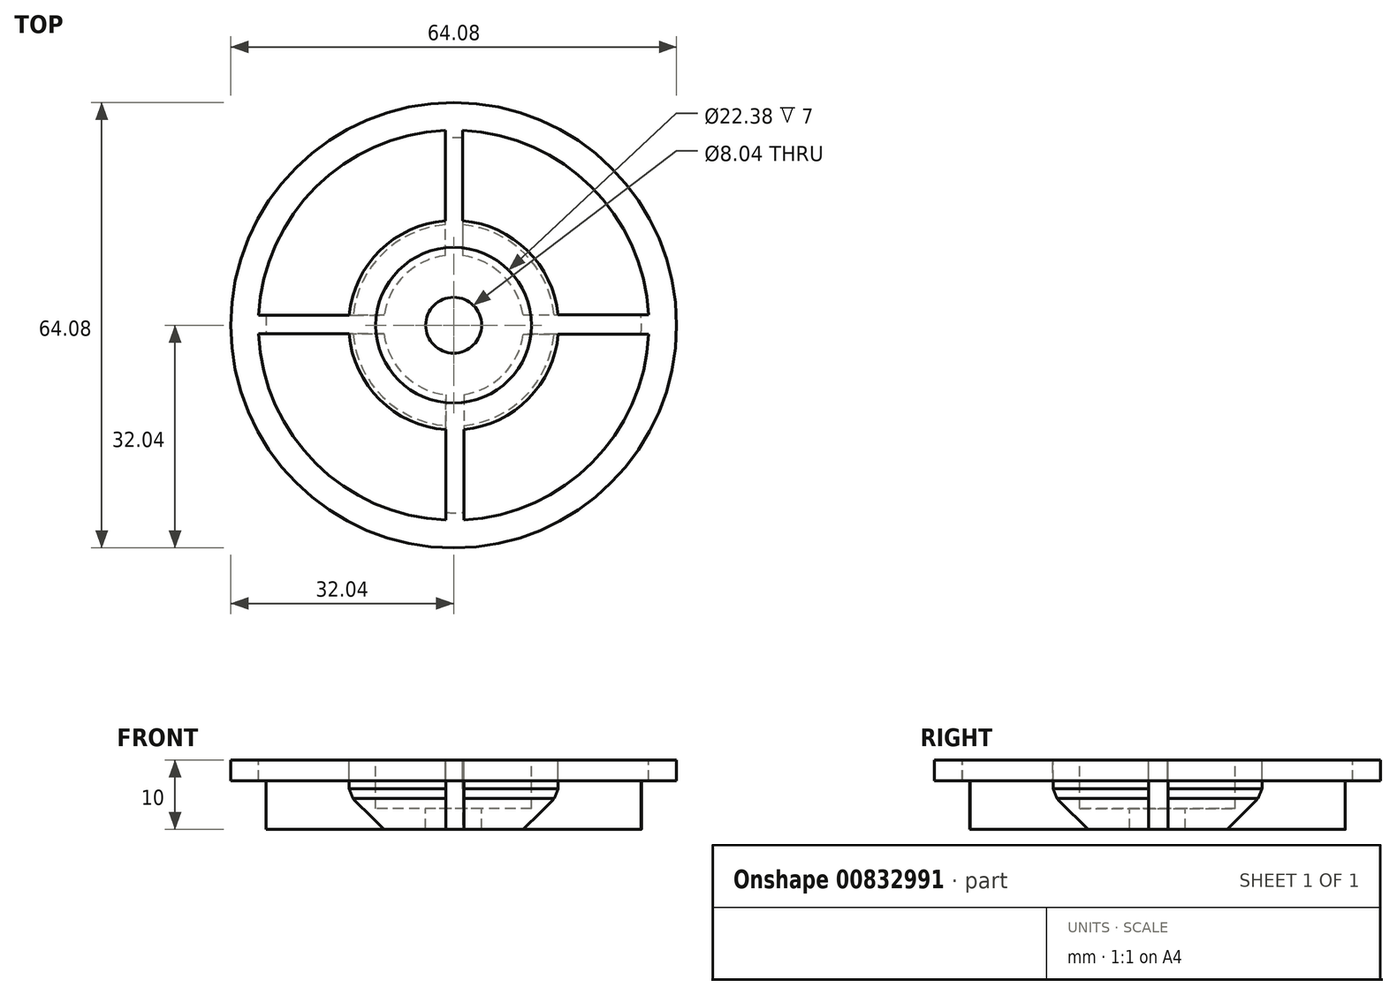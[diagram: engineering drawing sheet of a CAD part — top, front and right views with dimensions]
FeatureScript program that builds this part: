
annotation { "Feature Type Name" : "Feature", "Feature Type Description" : "" }
export const myFeature = defineFeature(function(context is Context, id is Id, definition is map)
    precondition{}
    {
        {
            var Q0;
            Q0=qCreatedBy(makeId("Top.planeOp"),FACE);
            var sketch = newSketch(context, id + "F0", { "sketchPlane" : qUnion([Q0])});
            skCircle(sketch, "E0", {"center": v(0, 0) * mm, "radius": 26.99 * mm});
            skSolve(sketch);
        }
        {
            var Q0;
            Q0 = qSketchRegion(id + "F0", true);
            extrude(context, id + "F1", {"entities" : qUnion([Q0]), "depth" : 7 * mm, "offsetDistance" : 25 * mm});
        }
        {
            var Q0;
            Q0=makeQuery(id+"F1.opExtrude","CAP_FACE",FACE,{"disambiguationData":[OSD([sQuery(id+"F0.wireOp",EDGE,"E0")])],"isStart":false});
            var sketch = newSketch(context, id + "F2", { "sketchPlane" : qUnion([Q0])});
            skCircle(sketch, "E1", {"center": v(0, 0) * mm, "radius": 32.04 * mm});
            skSolve(sketch);
        }
        {
            var Q0;
            Q0=makeQuery(id+"F2.imprint","IMPRINT",FACE,{"disambiguationData":[TD([[makeQuery(id+"F2.imprint","IMPRINT",EDGE,{"derivedFrom":sQuery(id+"F2.wireOp",EDGE,"E1")}),1.0]])]});
            var Q1;
            Q1=makeQuery(id+"F2.imprint","IMPRINT",FACE,{"disambiguationData":[TD([[makeQuery(id+"F2.imprint","IMPRINT",EDGE,{"derivedFrom":makeQuery(id+"F1.opExtrude","CAP_EDGE",EDGE,{"disambiguationData":[OSD([sQuery(id+"F0.wireOp",EDGE,"E0")])],"isStart":false})}),1.0]])]});
            extrude(context, id + "F3", {"entities" : qUnion([Q0, Q1]), "operationType" : NewBodyOperationType.ADD, "depth" : 3 * mm, "offsetDistance" : 25 * mm});
        }
        {
            var Q0;
            Q0=makeQuery(id+"F3.opExtrude","CAP_FACE",FACE,{"disambiguationData":[OSD([sQuery(id+"F2.wireOp",EDGE,"E1")])],"isStart":false});
            var sketch = newSketch(context, id + "F4", { "sketchPlane" : qUnion([Q0])});
            skCircle(sketch, "E2", {"center": v(0, 0) * mm, "radius": 11.2 * mm});
            skSolve(sketch);
        }
        {
            var Q0;
            Q0 = qSketchRegion(id + "F4", true);
            extrude(context, id + "F5", {"entities" : qUnion([Q0]), "operationType" : NewBodyOperationType.REMOVE, "oppositeDirection" : true, "depth" : 7 * mm, "offsetDistance" : 25 * mm});
        }
        {
            var Q0;
            Q0=makeQuery(id+"F5.boolean.opBoolean","COPY",FACE,{"derivedFrom":makeQuery(id+"F5.opExtrude","CAP_FACE",FACE,{"disambiguationData":[OSD([sQuery(id+"F4.wireOp",EDGE,"E2")])],"isStart":false})});
            var sketch = newSketch(context, id + "F6", { "sketchPlane" : qUnion([Q0])});
            skCircle(sketch, "E3", {"center": v(0, 0) * mm, "radius": 4.02 * mm});
            skSolve(sketch);
        }
        {
            var Q0;
            Q0 = qSketchRegion(id + "F6", true);
            extrude(context, id + "F7", {"entities" : qUnion([Q0]), "operationType" : NewBodyOperationType.REMOVE, "oppositeDirection" : true, "depth" : 25 * mm, "offsetDistance" : 25 * mm});
        }
        {
            var Q0;
            Q0=makeQuery(id+"F3.opExtrude","CAP_FACE",FACE,{"disambiguationData":[OSD([sQuery(id+"F2.wireOp",EDGE,"E1")])],"isStart":false});
            var sketch = newSketch(context, id + "F8", { "sketchPlane" : qUnion([Q0])});
            skArc(sketch, "E4", {"start": v(-15.03, -1.26) * mm, "mid": v(-10.63, -10.7) * mm, "end": v(-1.15, -15.04) * mm});
            skArc(sketch, "E5", {"start": v(-28.04, -1.26) * mm, "mid": v(-19.8, -19.88) * mm, "end": v(-1.15, -28.04) * mm});
            skLineSegment(sketch, "E6", {"start": v(1.48, -15.01) * mm, "end": v(1.48, -28.03) * mm});
            skLineSegment(sketch, "E7", {"start": v(-1.15, -15.04) * mm, "end": v(-1.15, -28.04) * mm});
            skLineSegment(sketch, "E8", {"start": v(15.03, -1.26) * mm, "end": v(28.04, -1.26) * mm});
            skLineSegment(sketch, "E9", {"start": v(15, 1.52) * mm, "end": v(28.02, 1.52) * mm});
            skLineSegment(sketch, "E10", {"start": v(-1.22, 15.03) * mm, "end": v(-1.22, 28.04) * mm});
            skLineSegment(sketch, "E11", {"start": v(1.3, 28.04) * mm, "end": v(1.3, 15.03) * mm});
            skLineSegment(sketch, "E12", {"start": v(-15.01, 1.44) * mm, "end": v(-28.03, 1.44) * mm});
            skLineSegment(sketch, "E13", {"start": v(-28.04, -1.26) * mm, "end": v(-15.03, -1.26) * mm});
            skPoint(sketch, "E14.start.orphan", {"position": v(-15.08, 0) * mm});
            skArc(sketch, "E15.trimOffspring", {"start": v(-1.22, 15.03) * mm, "mid": v(-10.58, 10.74) * mm, "end": v(-15.01, 1.44) * mm});
            skPoint(sketch, "E16.orphan", {"position": v(0, 15.08) * mm});
            skArc(sketch, "E17.trimOffspring", {"start": v(-1.22, 28.04) * mm, "mid": v(-19.77, 19.92) * mm, "end": v(-28.03, 1.44) * mm});
            skArc(sketch, "E18.trimOffspring", {"start": v(15, 1.52) * mm, "mid": v(10.58, 10.74) * mm, "end": v(1.3, 15.03) * mm});
            skPoint(sketch, "E19.start.orphan", {"position": v(15.08, 0) * mm});
            skArc(sketch, "E20.trimOffspring", {"start": v(28.02, 1.52) * mm, "mid": v(19.77, 19.92) * mm, "end": v(1.3, 28.04) * mm});
            skArc(sketch, "E21.trimOffspring", {"start": v(1.48, -28.03) * mm, "mid": v(19.92, -19.77) * mm, "end": v(28.04, -1.26) * mm});
            skPoint(sketch, "E22.start.orphan", {"position": v(0, -15.08) * mm});
            skArc(sketch, "E23.trimOffspring", {"start": v(1.48, -15.01) * mm, "mid": v(10.74, -10.59) * mm, "end": v(15.03, -1.26) * mm});
            skSolve(sketch);
        }
        {
            var Q0;
            Q0=makeQuery(id+"F8.imprint","IMPRINT",FACE,{"disambiguationData":[TD([[makeQuery(id+"F8.imprint","IMPRINT",EDGE,{"derivedFrom":sQuery(id+"F8.wireOp",EDGE,"E10")}),1.0]])]});
            var Q1;
            Q1=makeQuery(id+"F8.imprint","IMPRINT",FACE,{"disambiguationData":[TD([[makeQuery(id+"F8.imprint","IMPRINT",EDGE,{"derivedFrom":sQuery(id+"F8.wireOp",EDGE,"E9")}),1.0]])]});
            var Q2;
            Q2=makeQuery(id+"F8.imprint","IMPRINT",FACE,{"disambiguationData":[TD([[makeQuery(id+"F8.imprint","IMPRINT",EDGE,{"derivedFrom":sQuery(id+"F8.wireOp",EDGE,"E6")}),1.0]])]});
            var Q3;
            Q3=makeQuery(id+"F8.imprint","IMPRINT",FACE,{"disambiguationData":[TD([[makeQuery(id+"F8.imprint","IMPRINT",EDGE,{"derivedFrom":sQuery(id+"F8.wireOp",EDGE,"E4")}),-1.0]])]});
            extrude(context, id + "F9", {"entities" : qUnion([Q0, Q1, Q2, Q3]), "operationType" : NewBodyOperationType.REMOVE, "oppositeDirection" : true, "depth" : 25 * mm, "offsetDistance" : 25 * mm});
        }
        {
            var Q0;
            Q0=makeQuery(id+"F9.boolean.opBoolean","INTERSECT",EDGE,{"derivedFrom":[makeQuery(id+"F1.opExtrude","CAP_FACE",FACE,{"disambiguationData":[OSD([sQuery(id+"F0.wireOp",EDGE,"E0")])],"isStart":true}),makeQuery(id+"F9.opExtrude","SWEPT_FACE",FACE,{"disambiguationData":[OSD([sQuery(id+"F8.wireOp",EDGE,"E15.trimOffspring")])]})]});
            var Q1;
            Q1=makeQuery(id+"F9.boolean.opBoolean","INTERSECT",EDGE,{"derivedFrom":[makeQuery(id+"F1.opExtrude","CAP_FACE",FACE,{"disambiguationData":[OSD([sQuery(id+"F0.wireOp",EDGE,"E0")])],"isStart":true}),makeQuery(id+"F9.opExtrude","SWEPT_FACE",FACE,{"disambiguationData":[OSD([sQuery(id+"F8.wireOp",EDGE,"E18.trimOffspring")])]})]});
            var Q2;
            Q2=makeQuery(id+"F9.boolean.opBoolean","INTERSECT",EDGE,{"derivedFrom":[makeQuery(id+"F1.opExtrude","CAP_FACE",FACE,{"disambiguationData":[OSD([sQuery(id+"F0.wireOp",EDGE,"E0")])],"isStart":true}),makeQuery(id+"F9.opExtrude","SWEPT_FACE",FACE,{"disambiguationData":[OSD([sQuery(id+"F8.wireOp",EDGE,"E4")])]})]});
            var Q3;
            Q3=makeQuery(id+"F9.boolean.opBoolean","INTERSECT",EDGE,{"derivedFrom":[makeQuery(id+"F1.opExtrude","CAP_FACE",FACE,{"disambiguationData":[OSD([sQuery(id+"F0.wireOp",EDGE,"E0")])],"isStart":true}),makeQuery(id+"F9.opExtrude","SWEPT_FACE",FACE,{"disambiguationData":[OSD([sQuery(id+"F8.wireOp",EDGE,"E23.trimOffspring")])]})]});
            chamfer(context, id + "F10", {"entities" : qUnion([Q0, Q1, Q2, Q3]), "width" : 5 * mm, "tangentPropagation" : true});
        }
        {
            var Q0;
            {var subQ0=makeQuery(id+"F9.opExtrude","SWEPT_FACE",FACE,{"disambiguationData":[OSD([sQuery(id+"F8.wireOp",EDGE,"E23.trimOffspring")])]});Q0=makeQuery(id+"F10.opChamfer","BLEND_EDGE",EDGE,{"blendedFrom":[makeQuery(id+"F9.boolean.opBoolean","INTERSECT",EDGE,{"derivedFrom":[makeQuery(id+"F1.opExtrude","CAP_FACE",FACE,{"disambiguationData":[OSD([sQuery(id+"F0.wireOp",EDGE,"E0")])],"isStart":true}),subQ0]}),makeQuery(id+"F9.boolean.opBoolean","COPY",FACE,{"derivedFrom":subQ0})],"blendedInto":[makeQuery(id+"F9.boolean.opBoolean","COPY",FACE,{"derivedFrom":subQ0})]});}
            var Q1;
            {var subQ0=makeQuery(id+"F9.opExtrude","SWEPT_FACE",FACE,{"disambiguationData":[OSD([sQuery(id+"F8.wireOp",EDGE,"E4")])]});Q1=makeQuery(id+"F10.opChamfer","BLEND_EDGE",EDGE,{"blendedFrom":[makeQuery(id+"F9.boolean.opBoolean","INTERSECT",EDGE,{"derivedFrom":[makeQuery(id+"F1.opExtrude","CAP_FACE",FACE,{"disambiguationData":[OSD([sQuery(id+"F0.wireOp",EDGE,"E0")])],"isStart":true}),subQ0]}),makeQuery(id+"F9.boolean.opBoolean","COPY",FACE,{"derivedFrom":subQ0})],"blendedInto":[makeQuery(id+"F9.boolean.opBoolean","COPY",FACE,{"derivedFrom":subQ0})]});}
            var Q2;
            {var subQ0=makeQuery(id+"F9.opExtrude","SWEPT_FACE",FACE,{"disambiguationData":[OSD([sQuery(id+"F8.wireOp",EDGE,"E18.trimOffspring")])]});Q2=makeQuery(id+"F10.opChamfer","BLEND_EDGE",EDGE,{"blendedFrom":[makeQuery(id+"F9.boolean.opBoolean","INTERSECT",EDGE,{"derivedFrom":[makeQuery(id+"F1.opExtrude","CAP_FACE",FACE,{"disambiguationData":[OSD([sQuery(id+"F0.wireOp",EDGE,"E0")])],"isStart":true}),subQ0]}),makeQuery(id+"F9.boolean.opBoolean","COPY",FACE,{"derivedFrom":subQ0})],"blendedInto":[makeQuery(id+"F9.boolean.opBoolean","COPY",FACE,{"derivedFrom":subQ0})]});}
            var Q3;
            {var subQ0=makeQuery(id+"F9.opExtrude","SWEPT_FACE",FACE,{"disambiguationData":[OSD([sQuery(id+"F8.wireOp",EDGE,"E15.trimOffspring")])]});Q3=makeQuery(id+"F10.opChamfer","BLEND_EDGE",EDGE,{"blendedFrom":[makeQuery(id+"F9.boolean.opBoolean","INTERSECT",EDGE,{"derivedFrom":[makeQuery(id+"F1.opExtrude","CAP_FACE",FACE,{"disambiguationData":[OSD([sQuery(id+"F0.wireOp",EDGE,"E0")])],"isStart":true}),subQ0]}),makeQuery(id+"F9.boolean.opBoolean","COPY",FACE,{"derivedFrom":subQ0})],"blendedInto":[makeQuery(id+"F9.boolean.opBoolean","COPY",FACE,{"derivedFrom":subQ0})]});}
            chamfer(context, id + "F11", {"entities" : qUnion([Q0, Q1, Q2, Q3]), "width" : 2 * mm, "tangentPropagation" : true});
        }
    });
